# Revit family: AFB-C_Vertical_Wall_Mount
name_source: partatom
category: Mechanical Equipment
units: mm (PartAtom-declared; Revit-internal decimal feet)

## family parameters
Always vertical = Yes
Cut with Voids When Loaded = No
Part Type = Normal
Room Calculation Point = No
Round Connector Dimension = Use Radius
Shared = No
Work Plane-Based = No

## types (11) — shared parameters
0 = 0' - 0"
1" = 0' - 1"
1.5 = 0' - 1 1/2"
2" = 0' - 2"
2' = 2' - 0"
3" = 0' - 3"
30 = 30.00°
4" = 0' - 4"
60 = 60.00°
Manufacturer = Loren Cook Company
Model = AFB-C
ONE EIGTH = 0' - 0 1/8"
P = 0' - 0 9/16"
P/2 = 0' - 0 9/32"
Type Comments = Tube Axial Fan Vertical Wall Mount Belt Drive Arrangement 9
URL = www.lorencook.com

## per-type parameters (varying)
- 12_AFB-C_VERT_WALL: (A+.25")/2=0' - 6 9/16"; (E-.25")/2=0' - 10 7/8"; (H-(A/2))/2=0' - 9 3/32"; -(E-.25")/2=-0' - 10 7/8"; -E/2=-0' - 11"; 2L=0' - 1 7/8"; A=1' - 0 7/8"; A/2=0' - 6 7/16"; A/3=0' - 5 5/32"; B=1' - 3 5/8"; B/2=0' - 7 13/16"; C=1' - 2 5/8"; C/2=0' - 7 5/16"; C/2+J=1' - 5 1/16"; E=1' - 10"; E-2"=-1' - 8"; E/2=0' - 11"; F=0' - 0 5/16"; F/2=0' - 0 5/32"; G=6' - 0"; H=2' - 0 5/8"; H+J=2' - 10 3/8"; H-(A/2)=1' - 6 3/16"; J=0' - 9 3/4"; J-(C/2)=0' - 2 7/16"; J-.125"=0' - 9 5/8"; K=1' - 8 1/8"; K/2=0' - 10 1/16"; L=0' - 0 15/16"; M=1' - 4"; M/2=0' - 8"; N=0' - 6"
- 16_AFB-C_VERT_WALL: (A+.25")/2=0' - 8 9/16"; (E-.25")/2=1' - 0 3/8"; (H-(A/2))/2=0' - 10 27/32"; -(E-.25")/2=-1' - 0 3/8"; -E/2=-1' - 0 1/2"; 2L=0' - 1 7/8"; A=1' - 4 7/8"; A/2=0' - 8 7/16"; A/3=0' - 6 3/4"; B=1' - 7 5/8"; B/2=0' - 9 13/16"; C=1' - 6 5/8"; C/2=0' - 9 5/16"; C/2+J=1' - 9 1/16"; E=2' - 1"; E-2"=-1' - 11"; E/2=1' - 0 1/2"; F=0' - 0 5/16"; F/2=0' - 0 5/32"; G=6' - 0"; H=2' - 6 1/8"; H+J=3' - 5 7/8"; H-(A/2)=1' - 9 11/16"; J=0' - 11 3/4"; J-(C/2)=0' - 2 7/16"; J-.125"=0' - 11 5/8"; K=1' - 11 1/8"; K/2=0' - 11 9/16"; L=0' - 0 15/16"; M=1' - 8"; M/2=0' - 10"; N=0' - 8"
- 24_AFB-C_VERT_WALL: (A+.25")/2=1' - 0 9/16"; (E-.25")/2=1' - 3 3/8"; (H-(A/2))/2=1' - 1 23/32"; -(E-.25")/2=-1' - 3 3/8"; -E/2=-1' - 3 1/2"; 2L=0' - 1 7/8"; A=2' - 0 7/8"; A/2=1' - 0 7/16"; A/3=0' - 9 15/16"; B=2' - 5 1/8"; B/2=1' - 2 9/16"; C=2' - 2 7/8"; C/2=1' - 1 7/16"; C/2+J=2' - 5 7/16"; E=2' - 7"; E-2"=-2' - 5"; E/2=1' - 3 1/2"; F=0' - 0 7/16"; F/2=0' - 0 7/32"; G=6' - 0"; H=3' - 3 7/8"; H+J=4' - 7 7/8"; H-(A/2)=2' - 3 7/16"; J=1' - 4"; J-(C/2)=0' - 2 9/16"; J-.125"=1' - 3 7/8"; K=2' - 5 1/8"; K/2=1' - 2 9/16"; L=0' - 0 15/16"; M=2' - 4 1/2"; M/2=1' - 2 1/4"; N=1' - 0 1/4"
- 28_AFB-C_VERT_WALL: (A+.25")/2=1' - 2 9/16"; (E-.25")/2=1' - 3 3/8"; (H-(A/2))/2=1' - 1 23/32"; -(E-.25")/2=-1' - 3 3/8"; -E/2=-1' - 3 1/2"; 2L=0' - 1 7/8"; A=2' - 4 7/8"; A/2=1' - 2 7/16"; A/3=0' - 11 9/16"; B=2' - 9 1/8"; B/2=1' - 4 9/16"; C=2' - 6 7/8"; C/2=1' - 3 7/16"; C/2+J=2' - 9 7/16"; E=2' - 7"; E-2"=-2' - 5"; E/2=1' - 3 1/2"; F=0' - 0 7/16"; F/2=0' - 0 7/32"; G=6' - 0"; H=3' - 5 7/8"; H+J=4' - 11 7/8"; H-(A/2)=2' - 3 7/16"; J=1' - 6"; J-(C/2)=0' - 2 9/16"; J-.125"=1' - 5 7/8"; K=2' - 5 1/8"; K/2=1' - 2 9/16"; L=0' - 0 15/16"; M=2' - 8 1/2"; M/2=1' - 4 1/4"; N=1' - 2 1/4"
- 32_AFB-C_VERT_WALL: (A+.25")/2=1' - 4 5/8"; (E-.25")/2=1' - 4 7/8"; (H-(A/2))/2=1' - 2 3/8"; -(E-.25")/2=-1' - 4 7/8"; -E/2=-1' - 5"; 2L=0' - 1 7/8"; A=2' - 9"; A/2=1' - 4 1/2"; A/3=1' - 1 3/16"; B=3' - 1 1/4"; B/2=1' - 6 5/8"; C=2' - 11"; C/2=1' - 5 1/2"; C/2+J=3' - 1 5/8"; E=2' - 10"; E-2"=-2' - 8"; E/2=1' - 5"; F=0' - 0 7/16"; F/2=0' - 0 7/32"; G=6' - 0"; H=3' - 9 1/4"; H+J=5' - 5 3/8"; H-(A/2)=2' - 4 3/4"; J=1' - 8 1/8"; J-(C/2)=0' - 2 5/8"; J-.125"=1' - 8"; K=2' - 8 1/8"; K/2=1' - 4 1/16"; L=0' - 0 15/16"; M=3' - 0 5/8"; M/2=1' - 6 5/16"; N=1' - 4 5/16"
- 36_AFB-C_VERT_WALL: (A+.25")/2=1' - 6 5/8"; (E-.25")/2=1' - 4 7/8"; (H-(A/2))/2=1' - 2 3/8"; -(E-.25")/2=-1' - 4 7/8"; -E/2=-1' - 5"; 2L=0' - 1 7/8"; A=3' - 1"; A/2=1' - 6 1/2"; A/3=1' - 2 13/16"; B=3' - 5 3/8"; B/2=1' - 8 11/16"; C=3' - 3"; C/2=1' - 7 1/2"; C/2+J=3' - 5 5/8"; E=2' - 10"; E-2"=-2' - 8"; E/2=1' - 5"; F=0' - 0 7/16"; F/2=0' - 0 7/32"; G=6' - 0"; H=3' - 11 1/4"; H+J=5' - 9 3/8"; H-(A/2)=2' - 4 3/4"; J=1' - 10 1/8"; J-(C/2)=0' - 2 5/8"; J-.125"=1' - 10"; K=2' - 8 1/8"; K/2=1' - 4 1/16"; L=0' - 0 15/16"; M=3' - 4 5/8"; M/2=1' - 8 5/16"; N=1' - 6 5/16"
- 44_AFB-C_VERT_WALL: (A+.25")/2=1' - 10 5/8"; (E-.25")/2=1' - 8 7/8"; (H-(A/2))/2=1' - 6 1/8"; -(E-.25")/2=-1' - 8 7/8"; -E/2=-1' - 9"; 2L=0' - 2"; A=3' - 9"; A/2=1' - 10 1/2"; A/3=1' - 6"; B=4' - 1 3/8"; B/2=2' - 0 11/16"; C=3' - 11 1/2"; C/2=1' - 11 3/4"; C/2+J=4' - 1 7/8"; E=3' - 6"; E-2"=-3' - 4"; E/2=1' - 9"; F=0' - 0 7/16"; F/2=0' - 0 7/32"; G=12' - 0"; H=4' - 10 3/4"; H+J=7' - 0 7/8"; H-(A/2)=3' - 0 1/4"; J=2' - 2 1/8"; J-(C/2)=0' - 2 3/8"; J-.125"=2' - 2"; K=3' - 4"; K/2=1' - 8"; L=0' - 1"; M=4' - 0 3/4"; M/2=2' - 0 3/8"; N=1' - 10 3/8"
- 48_AFB-C_VERT_WALL: (A+.25")/2=2' - 0 11/16"; (E-.25")/2=1' - 8 7/8"; (H-(A/2))/2=1' - 6 3/32"; -(E-.25")/2=-1' - 8 7/8"; -E/2=-1' - 9"; 2L=0' - 2"; A=4' - 1 1/8"; A/2=2' - 0 9/16"; A/3=1' - 7 21/32"; B=4' - 5 1/2"; B/2=2' - 2 3/4"; C=4' - 3 5/8"; C/2=2' - 1 13/16"; C/2+J=4' - 6 9/16"; E=3' - 6"; E-2"=-3' - 4"; E/2=1' - 9"; F=0' - 0 7/16"; F/2=0' - 0 7/32"; G=12' - 0"; H=5' - 0 3/4"; H+J=7' - 5 1/2"; H-(A/2)=3' - 0 3/16"; J=2' - 4 3/4"; J-(C/2)=0' - 2 15/16"; J-.125"=2' - 4 5/8"; K=3' - 4"; K/2=1' - 8"; L=0' - 1"; M=4' - 5 7/8"; M/2=2' - 2 15/16"; N=2' - 0 15/16"
- 54_AFB-C_VERT_WALL: (A+.25")/2=2' - 3 13/16"; (E-.25")/2=1' - 8 7/8"; (H-(A/2))/2=1' - 0 1/32"; -(E-.25")/2=-1' - 8 7/8"; -E/2=-1' - 9"; 2L=0' - 2 1/4"; A=4' - 7 3/8"; A/2=2' - 3 11/16"; A/3=1' - 10 5/32"; B=5' - 0 3/4"; B/2=2' - 6 3/8"; C=4' - 9 5/8"; C/2=2' - 4 13/16"; C/2+J=5' - 0 11/16"; E=3' - 6"; E-2"=-3' - 4"; E/2=1' - 9"; F=0' - 0 7/16"; F/2=0' - 0 7/32"; G=12' - 0"; H=4' - 3 3/4"; H+J=6' - 11 5/8"; H-(A/2)=2' - 0 1/16"; J=2' - 7 7/8"; J-(C/2)=0' - 3 1/16"; J-.125"=2' - 7 3/4"; K=3' - 3 3/4"; K/2=1' - 7 7/8"; L=0' - 1 1/8"; M=5' - 0 1/8"; M/2=2' - 6 1/16"; N=2' - 4 1/16"
- 60_AFB-C_VERT_WALL: (A+.25")/2=2' - 6 13/16"; (E-.25")/2=1' - 8 7/8"; (H-(A/2))/2=1' - 0 1/32"; -(E-.25")/2=-1' - 8 7/8"; -E/2=-1' - 9"; 2L=0' - 2 1/4"; A=5' - 1 3/8"; A/2=2' - 6 11/16"; A/3=2' - 0 9/16"; B=5' - 6 3/4"; B/2=2' - 9 3/8"; C=5' - 3 5/8"; C/2=2' - 7 13/16"; C/2+J=5' - 6 11/16"; E=3' - 6"; E-2"=-3' - 4"; E/2=1' - 9"; F=0' - 3"; F/2=0' - 1 1/2"; G=12' - 0"; H=4' - 6 3/4"; H+J=7' - 5 5/8"; H-(A/2)=2' - 0 1/16"; J=2' - 10 7/8"; J-(C/2)=0' - 3 1/16"; J-.125"=2' - 10 3/4"; K=3' - 3 3/4"; K/2=1' - 7 7/8"; L=0' - 1 1/8"; M=5' - 6 1/8"; M/2=2' - 9 1/16"; N=2' - 7 1/16"
- 18_AFB-C_VERT_WALL: (A+.25")/2=0' - 9 9/16"; (E-.25")/2=1' - 0 3/8"; (H-(A/2))/2=0' - 10 27/32"; -(E-.25")/2=-1' - 0 3/8"; -E/2=-1' - 0 1/2"; 2L=0' - 1 7/8"; A=1' - 6 7/8"; A/2=0' - 9 7/16"; A/3=0' - 7 9/16"; B=1' - 9 5/8"; B/2=0' - 10 13/16"; C=1' - 8 5/8"; C/2=0' - 10 5/16"; C/2+J=1' - 11 1/16"; E=2' - 1"; E-2"=-1' - 11"; E/2=1' - 0 1/2"; F=0' - 0 5/16"; F/2=0' - 0 5/32"; G=6' - 0"; H=2' - 7 1/8"; H+J=3' - 7 7/8"; H-(A/2)=1' - 9 11/16"; J=1' - 0 3/4"; J-(C/2)=0' - 2 7/16"; J-.125"=1' - 0 5/8"; K=1' - 11 1/8"; K/2=0' - 11 9/16"; L=0' - 0 15/16"; M=1' - 10"; M/2=0' - 11"; N=0' - 9"

## geometry (parser evidence)
native form markers: Sweep x1
no freeform markers — native parametric forms only
